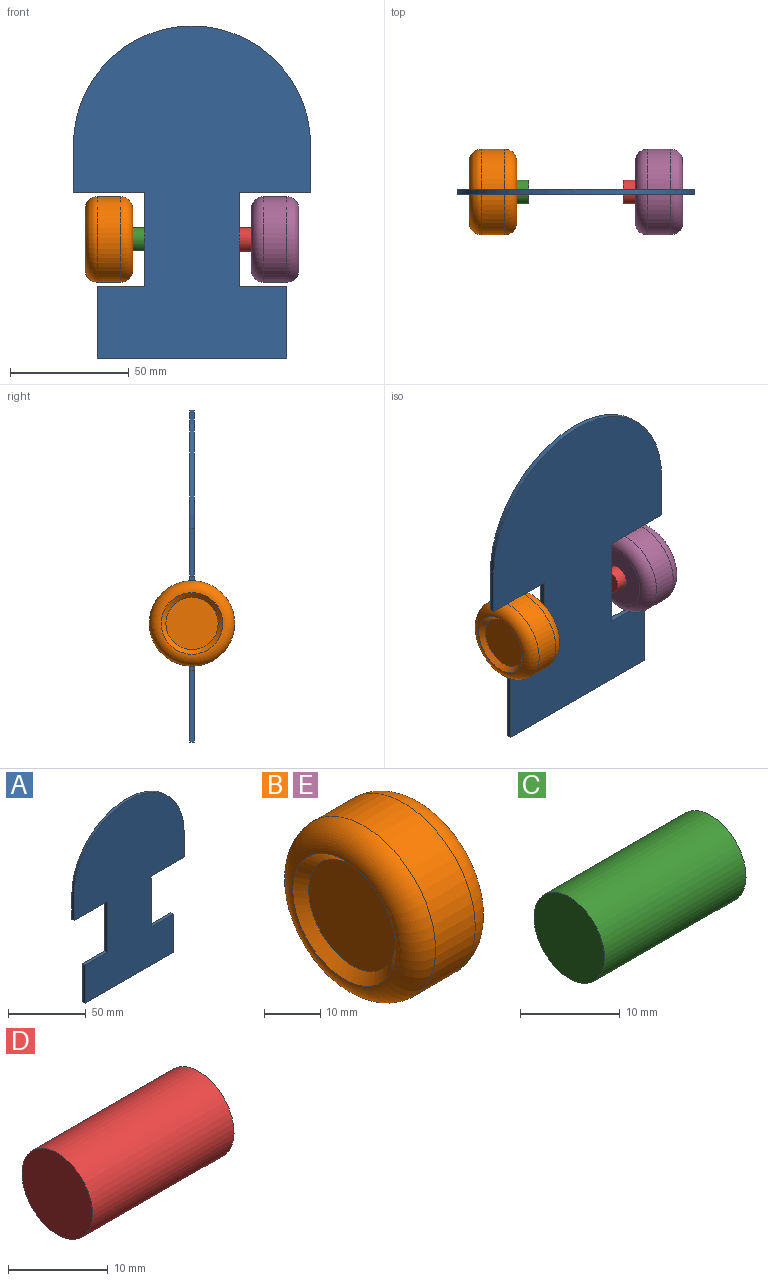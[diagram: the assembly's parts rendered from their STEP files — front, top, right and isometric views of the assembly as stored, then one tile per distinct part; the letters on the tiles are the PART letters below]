
ASSEMBLY  parts=5 mates=6
PART A: 14 faces, bbox 100x2x140 mm
  f0: plane 80x2mm, normal (0,0,-1), area 160mm2, adj f1,f11,f12,f13
  f1: plane 30x2mm, normal (1,0,0), area 60mm2, adj f0,f2,f12,f13
  f2: plane 20x2mm, normal (0,0,1), area 40mm2, adj f1,f3,f12,f13
  f3: plane 40x2mm, normal (1,0,0), area 80mm2, adj f2,f4,f12,f13
  f4: plane 30x2mm, normal (0,0,-1), area 60mm2, adj f3,f5,f12,f13
  f5: plane 20x2mm, normal (1,0,0), area 40mm2, adj f4,f6,f12,f13
  f6: cylinder r=50mm len=100mm, axis (0,-1,0), area 314.2mm2, adj f5,f7,f12,f13
  f7: plane 20x2mm, normal (-1,0,0), area 40mm2, adj f6,f8,f12,f13
  f8: plane 30x2mm, normal (0,0,-1), area 60mm2, adj f7,f9,f12,f13
  f9: plane 40x2mm, normal (-1,0,0), area 80mm2, adj f8,f10,f12,f13
  f10: plane 20x2mm, normal (0,0,1), area 40mm2, adj f9,f11,f12,f13
  f11: plane 30x2mm, normal (-1,0,0), area 60mm2, adj f0,f10,f12,f13
  f12: plane 140x100mm, normal (0,1,0), area 9927mm2, adj f0,f1,f2,f3,f4,f5,f6,f7
  f13: plane 140x100mm, normal (0,-1,0), area 9927mm2, adj f0,f1,f2,f3,f4,f5,f6,f7
PART B: 8 faces, bbox 20x39x39 mm
  f0: cylinder r=18mm len=36mm, axis (-1,0,0), area 1131mm2, adj f4,f5
  f1: plane 26x26mm, normal (1,0,0), area 452.4mm2, adj f2,f5
  f2: cylinder r=5mm len=15mm, axis (1,0,0), area 471.2mm2, adj f1,f3
  f3: plane 10x10mm, normal (1,0,0), area 78.5mm2, adj f2
  f4: torus R=13mm, axis (1,0,0), area 798.6mm2, adj f0,f7
  f5: torus R=13mm, axis (1,0,0), area 798.6mm2, adj f0,f1
  f6: plane 22x22mm, normal (-1,0,0), area 380.1mm2, adj f7
  f7: cone r=11mm half-angle=45deg, axis (-1,0,0), area 213.3mm2, adj f4,f6
PART C: 3 faces, bbox 20x10x10 mm
  f0: cylinder r=5mm len=20mm, axis (1,0,0), area 628.3mm2, adj f1,f2
  f1: plane 10x10mm, normal (-1,0,0), area 78.5mm2, adj f0
  f2: plane 10x10mm, normal (1,0,0), area 78.5mm2, adj f0
PART D: 3 faces, bbox 20x10x10 mm
  f0: cylinder r=5mm len=20mm, axis (-1,0,0), area 628.3mm2, adj f1,f2
  f1: plane 10x10mm, normal (1,0,0), area 78.5mm2, adj f0
  f2: plane 10x10mm, normal (-1,0,0), area 78.5mm2, adj f0
PART E: same geometry as B
PLACE A t=(-30.14,-18.91,-20.77)mm fixed
PLACE B t=(-75.14,-17.91,-20.77)mm
PLACE C t=(-30.14,-18.91,-20.77)mm
PLACE D t=(-30.14,-18.91,-20.77)mm
PLACE E rot(axis=(0,0,1),180deg) t=(14.86,-17.91,-20.77)mm
MATE fastened D.f0 <-> A.f3  axis (-1,0,0) through (-10.14,-17.91,-20.77)mm
MATE fastened B.f2 <-> C.f0  axis (1,0,0) through (-70.14,-17.91,-20.77)mm
MATE planar C.f0 <-> A.f9  axis (1,0,0) through (-50.14,-17.91,-20.77)mm
MATE slider C.f0 <-> D.f0  axis (1,0,0) through (-50.14,-17.91,-20.77)mm
MATE planar D.f0 <-> A.f3  axis (-1,0,0) through (-10.14,-17.91,-20.77)mm
MATE fastened E.f2 <-> D.f0  axis (-1,0,0) through (9.86,-17.91,-20.77)mm
